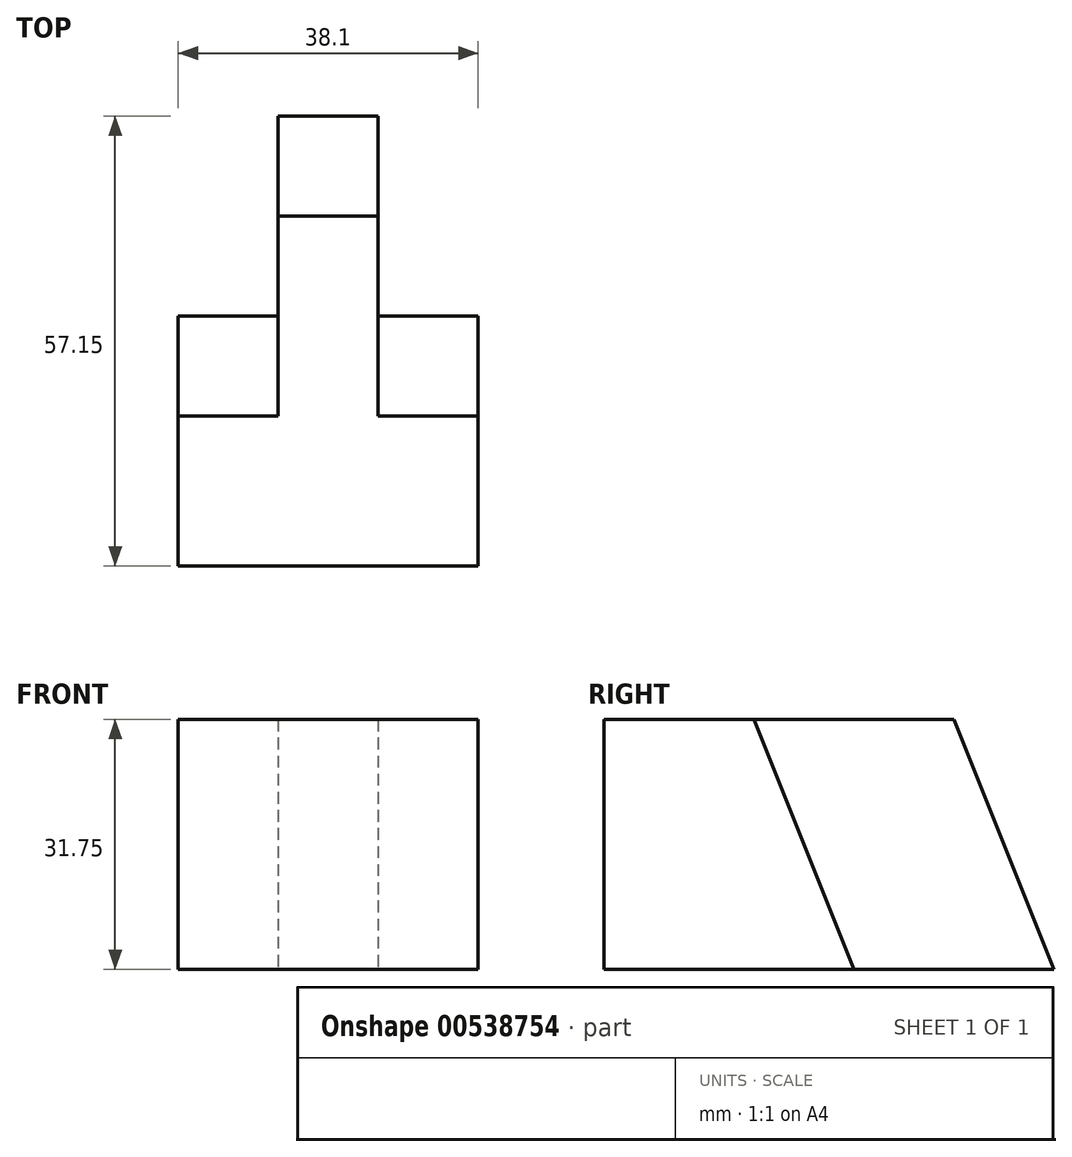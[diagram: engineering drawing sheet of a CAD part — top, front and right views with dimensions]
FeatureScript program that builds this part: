
annotation { "Feature Type Name" : "Feature", "Feature Type Description" : "" }
export const myFeature = defineFeature(function(context is Context, id is Id, definition is map)
    precondition{}
    {
        {
            var Q0;
            Q0=qCreatedBy(makeId("Right.planeOp"),FACE);
            var sketch = newSketch(context, id + "F0", { "sketchPlane" : qUnion([Q0])});
            skLineSegment(sketch, "E0", {"start": v(-71.17, 49.54) * mm, "end": v(-14.02, 49.54) * mm});
            skLineSegment(sketch, "E1", {"start": v(-14.02, 49.54) * mm, "end": v(-14.02, 17.79) * mm});
            skLineSegment(sketch, "E2", {"start": v(-14.02, 17.79) * mm, "end": v(-71.17, 17.79) * mm});
            skLineSegment(sketch, "E3", {"start": v(-71.17, 17.79) * mm, "end": v(-71.17, 49.54) * mm});
            skSolve(sketch);
        }
        {
            var Q0;
            Q0=makeQuery(id+"F0.imprint","IMPRINT",FACE,{"disambiguationData":[TD([[makeQuery(id+"F0.imprint","IMPRINT",EDGE,{"derivedFrom":sQuery(id+"F0.wireOp",EDGE,"E0")}),-1.0]])]});
            extrude(context, id + "F1", {"entities" : qUnion([Q0]), "depth" : 38.1 * mm, "offsetDistance" : 25.4 * mm});
        }
        {
            var Q0;
            Q0=makeQuery(id+"F1.opExtrude","CAP_FACE",FACE,{"disambiguationData":[OSD([sQuery(id+"F0.wireOp",EDGE,"E0"),sQuery(id+"F0.wireOp",EDGE,"E1"),sQuery(id+"F0.wireOp",EDGE,"E2"),sQuery(id+"F0.wireOp",EDGE,"E3")])],"isStart":false});
            var sketch = newSketch(context, id + "F2", { "sketchPlane" : qUnion([Q0])});
            skLineSegment(sketch, "E4", {"start": v(-26.72, 49.54) * mm, "end": v(-14.02, 17.79) * mm});
            skLineSegment(sketch, "E5", {"start": v(-26.72, 49.54) * mm, "end": v(-52.12, 49.54) * mm});
            skLineSegment(sketch, "E6", {"start": v(-52.12, 49.54) * mm, "end": v(-39.42, 17.79) * mm});
            skLineSegment(sketch, "E7", {"start": v(-39.42, 17.79) * mm, "end": v(-14.02, 17.79) * mm});
            skSolve(sketch);
        }
        {
            var Q0;
            Q0=makeQuery(id+"F2.imprint","IMPRINT",FACE,{"disambiguationData":[TD([[makeQuery(id+"F2.imprint","IMPRINT",EDGE,{"derivedFrom":sQuery(id+"F2.wireOp",EDGE,"E4")}),-1.0]])]});
            extrude(context, id + "F3", {"entities" : qUnion([Q0]), "operationType" : NewBodyOperationType.REMOVE, "oppositeDirection" : true, "depth" : 12.7 * mm, "offsetDistance" : 25.4 * mm});
        }
        {
            var Q0;
            {var subQ0=sQuery(id+"F0.wireOp",EDGE,"E0");var subQ1=sQuery(id+"F0.wireOp",EDGE,"E1");Q0=makeQuery(id+"F3.boolean.opBoolean","SPLIT",FACE,{"disambiguationData":[TD([makeQuery(id+"F1.opExtrude","SWEPT_FACE",FACE,{"disambiguationData":[OSD([subQ1])]})])],"derivedFrom":makeQuery(id+"F1.opExtrude","CAP_FACE",FACE,{"disambiguationData":[OSD([subQ0,subQ1,sQuery(id+"F0.wireOp",EDGE,"E2"),sQuery(id+"F0.wireOp",EDGE,"E3")])],"isStart":false})});}
            extrude(context, id + "F4", {"entities" : qUnion([Q0]), "operationType" : NewBodyOperationType.REMOVE, "oppositeDirection" : true, "depth" : 38.1 * mm, "offsetDistance" : 25.4 * mm});
        }
        {
            var Q0;
            Q0=makeQuery(id+"F1.opExtrude","CAP_FACE",FACE,{"disambiguationData":[OSD([sQuery(id+"F0.wireOp",EDGE,"E0"),sQuery(id+"F0.wireOp",EDGE,"E1"),sQuery(id+"F0.wireOp",EDGE,"E2"),sQuery(id+"F0.wireOp",EDGE,"E3")])],"isStart":true});
            var sketch = newSketch(context, id + "F5", { "sketchPlane" : qUnion([Q0])});
            skLineSegment(sketch, "E8", {"start": v(52.12, 49.54) * mm, "end": v(39.42, 17.79) * mm});
            skLineSegment(sketch, "E9", {"start": v(39.42, 17.79) * mm, "end": v(14.02, 17.79) * mm});
            skLineSegment(sketch, "E10", {"start": v(14.02, 17.79) * mm, "end": v(26.72, 49.54) * mm});
            skLineSegment(sketch, "E11", {"start": v(26.72, 49.54) * mm, "end": v(52.12, 49.54) * mm});
            skSolve(sketch);
        }
        {
            var Q0;
            Q0=makeQuery(id+"F5.imprint","IMPRINT",FACE,{"disambiguationData":[TD([[makeQuery(id+"F5.imprint","IMPRINT",EDGE,{"derivedFrom":sQuery(id+"F5.wireOp",EDGE,"E8")}),-1.0]])]});
            extrude(context, id + "F6", {"entities" : qUnion([Q0]), "operationType" : NewBodyOperationType.REMOVE, "oppositeDirection" : true, "depth" : 12.7 * mm, "offsetDistance" : 25.4 * mm});
        }
    });
